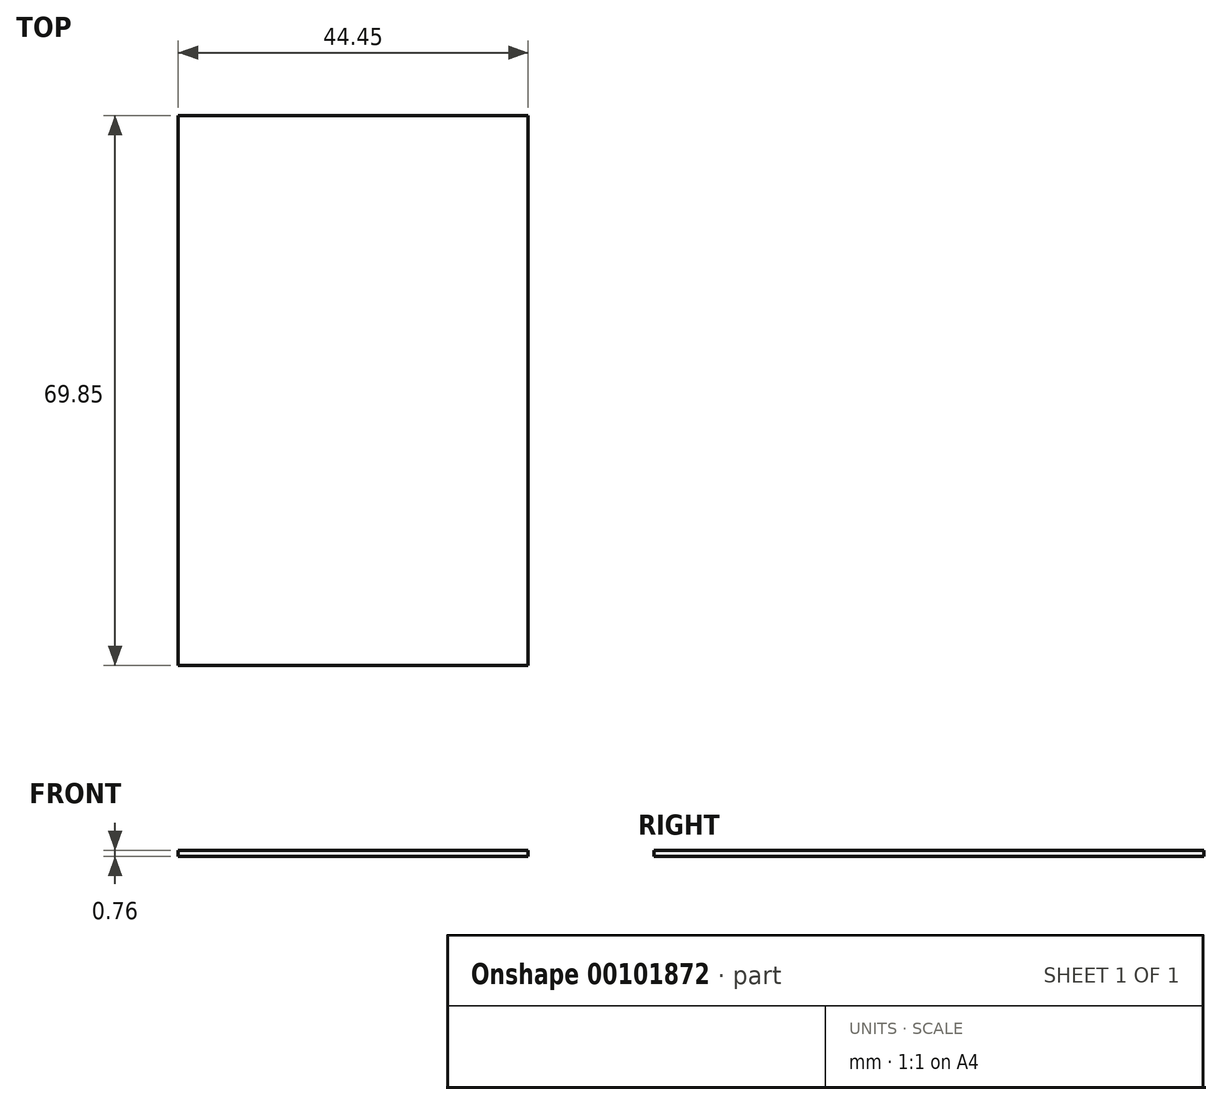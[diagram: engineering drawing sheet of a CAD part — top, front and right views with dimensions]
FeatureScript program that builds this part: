
annotation { "Feature Type Name" : "Feature", "Feature Type Description" : "" }
export const myFeature = defineFeature(function(context is Context, id is Id, definition is map)
    precondition{}
    {
        {
            var Q0;
            Q0=qCreatedBy(makeId("Top.planeOp"),FACE);
            var sketch = newSketch(context, id + "F0", { "sketchPlane" : qUnion([Q0])});
            skLineSegment(sketch, "E0.bottom", {"start": v(0, 0) * mm, "end": v(44.45, 0) * mm});
            skLineSegment(sketch, "E0.top", {"start": v(0, 69.85) * mm, "end": v(44.45, 69.85) * mm});
            skLineSegment(sketch, "E0.left", {"start": v(0, 0) * mm, "end": v(0, 69.85) * mm});
            skLineSegment(sketch, "E0.right", {"start": v(44.45, 0) * mm, "end": v(44.45, 69.85) * mm});
            skSolve(sketch);
        }
        {
            var Q0;
            Q0=makeQuery(id+"F0.imprint","IMPRINT",FACE,{"disambiguationData":[TD([[makeQuery(id+"F0.imprint","IMPRINT",EDGE,{"derivedFrom":sQuery(id+"F0.wireOp",EDGE,"E0.bottom")}),1.0]])]});
            extrude(context, id + "F1", {"entities" : qUnion([Q0]), "depth" : 0.76 * mm});
        }
    });
